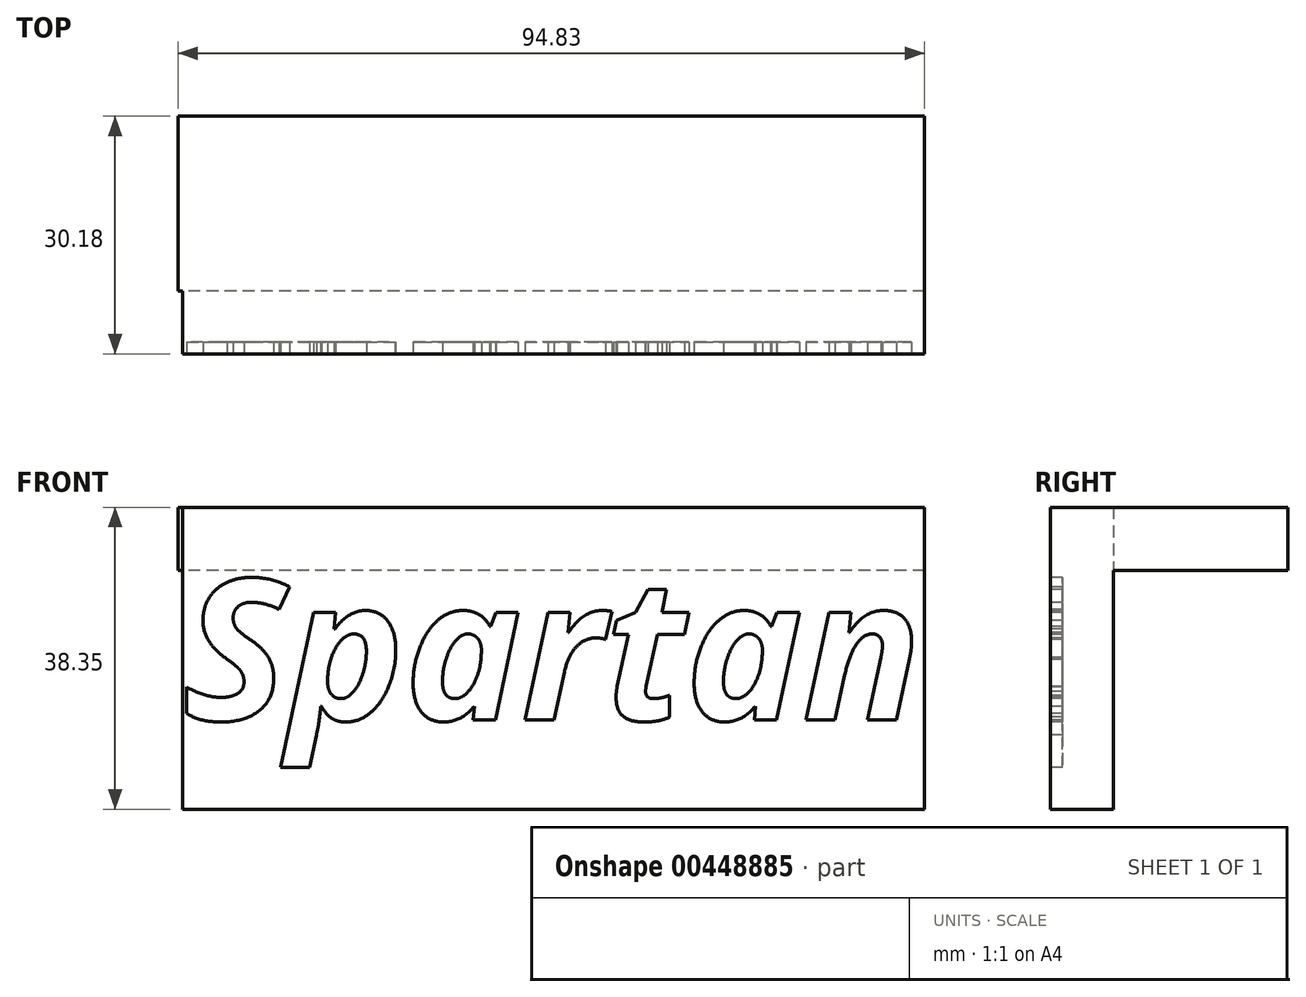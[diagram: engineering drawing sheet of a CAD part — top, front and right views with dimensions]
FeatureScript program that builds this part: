
annotation { "Feature Type Name" : "Feature", "Feature Type Description" : "" }
export const myFeature = defineFeature(function(context is Context, id is Id, definition is map)
    precondition{}
    {
        {
            var Q0;
            Q0=qCreatedBy(makeId("Front.planeOp"),FACE);
            var sketch = newSketch(context, id + "F0", { "sketchPlane" : qUnion([Q0])});
            skLineSegment(sketch, "E0.bottom", {"start": v(0, 0) * mm, "end": v(-94.24, 0) * mm});
            skLineSegment(sketch, "E0.top", {"start": v(0, -38.35) * mm, "end": v(-94.24, -38.35) * mm});
            skLineSegment(sketch, "E0.left", {"start": v(0, 0) * mm, "end": v(0, -38.35) * mm});
            skLineSegment(sketch, "E0.right", {"start": v(-94.24, 0) * mm, "end": v(-94.24, -38.35) * mm});
            skSolve(sketch);
        }
        {
            var Q0;
            Q0=makeQuery(id+"F0.imprint","IMPRINT",FACE,{"disambiguationData":[TD([[makeQuery(id+"F0.imprint","IMPRINT",EDGE,{"derivedFrom":sQuery(id+"F0.wireOp",EDGE,"E0.bottom")}),1.0]])]});
            extrude(context, id + "F1", {"entities" : qUnion([Q0]), "depth" : 8 * mm});
        }
        {
            var Q0;
            Q0=qCreatedBy(makeId("Top.planeOp"),FACE);
            var sketch = newSketch(context, id + "F2", { "sketchPlane" : qUnion([Q0])});
            skLineSegment(sketch, "E1.bottom", {"start": v(0, 0) * mm, "end": v(-94.83, 0) * mm});
            skLineSegment(sketch, "E1.top", {"start": v(0, 22.18) * mm, "end": v(-94.83, 22.18) * mm});
            skLineSegment(sketch, "E1.left", {"start": v(0, 0) * mm, "end": v(0, 22.18) * mm});
            skLineSegment(sketch, "E1.right", {"start": v(-94.83, 0) * mm, "end": v(-94.83, 22.18) * mm});
            skSolve(sketch);
        }
        {
            var Q0;
            Q0=makeQuery(id+"F2.imprint","IMPRINT",FACE,{"disambiguationData":[TD([[makeQuery(id+"F2.imprint","IMPRINT",EDGE,{"derivedFrom":sQuery(id+"F2.wireOp",EDGE,"E1.bottom")}),-1.0]])]});
            extrude(context, id + "F3", {"entities" : qUnion([Q0]), "operationType" : NewBodyOperationType.ADD, "depth" : -8 * mm});
        }
        {
            var Q0;
            Q0=makeQuery(id+"F1.opExtrude","CAP_FACE",FACE,{"disambiguationData":[OSD([sQuery(id+"F0.wireOp",EDGE,"E0.bottom"),sQuery(id+"F0.wireOp",EDGE,"E0.top"),sQuery(id+"F0.wireOp",EDGE,"E0.left"),sQuery(id+"F0.wireOp",EDGE,"E0.right")])],"isStart":false});
            var sketch = newSketch(context, id + "F4", { "sketchPlane" : qUnion([Q0])});
            skText(sketch, "E2", { "text": "Spartan", "fontName": "OpenSans-BoldItalic.ttf"});
            const initialGuessF4  = {"E2": [-0.09424, -0.02703, 1, 0, 0.01803]};
            skSetInitialGuess(sketch, initialGuessF4);
            skSolve(sketch);
        }
        {
            var Q0;
            Q0 = qSketchRegion(id + "F4", true);
            extrude(context, id + "F5", {"entities" : qUnion([Q0]), "operationType" : NewBodyOperationType.REMOVE, "oppositeDirection" : true, "depth" : 1.5 * mm});
        }
    });
